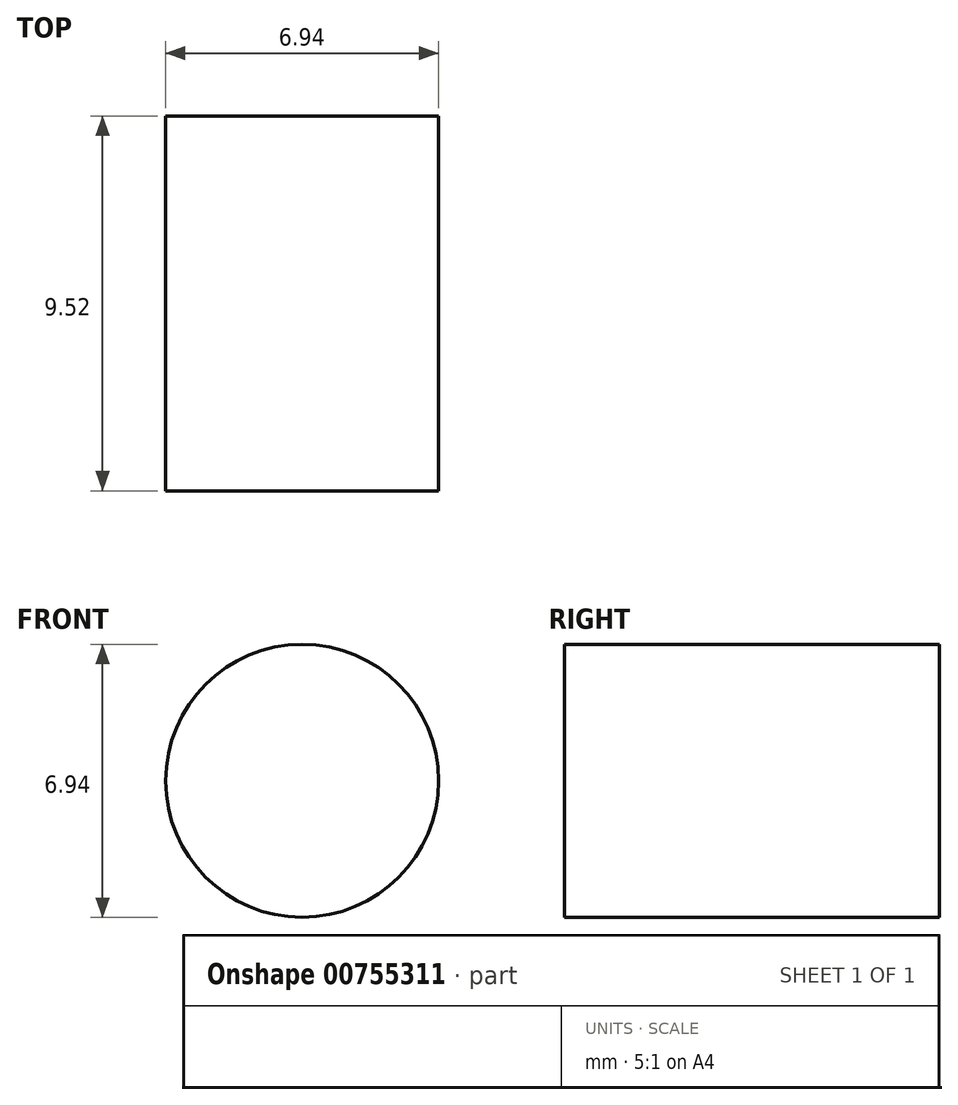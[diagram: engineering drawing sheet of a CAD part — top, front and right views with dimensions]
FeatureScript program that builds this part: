
annotation { "Feature Type Name" : "Feature", "Feature Type Description" : "" }
export const myFeature = defineFeature(function(context is Context, id is Id, definition is map)
    precondition{}
    {
        {
            var Q0;
            Q0=qCreatedBy(makeId("Front.planeOp"),FACE);
            var sketch = newSketch(context, id + "F0", { "sketchPlane" : qUnion([Q0])});
            skCircle(sketch, "E0", {"center": v(0, 0) * mm, "radius": 3.5 * mm});
            skCircle(sketch, "E1", {"center": v(0, 0) * mm, "radius": 3.47 * mm});
            skSolve(sketch);
        }
        {
            var Q0;
            Q0=makeQuery(id+"F0.imprint","IMPRINT",FACE,{"disambiguationData":[TD([[makeQuery(id+"F0.imprint","IMPRINT",EDGE,{"derivedFrom":sQuery(id+"F0.wireOp",EDGE,"E1")}),1.0]])]});
            extrude(context, id + "F1", {"entities" : qUnion([Q0]), "depth" : 9.52 * mm, "offsetDistance" : 25.4 * mm, "symmetric" : true});
        }
    });
